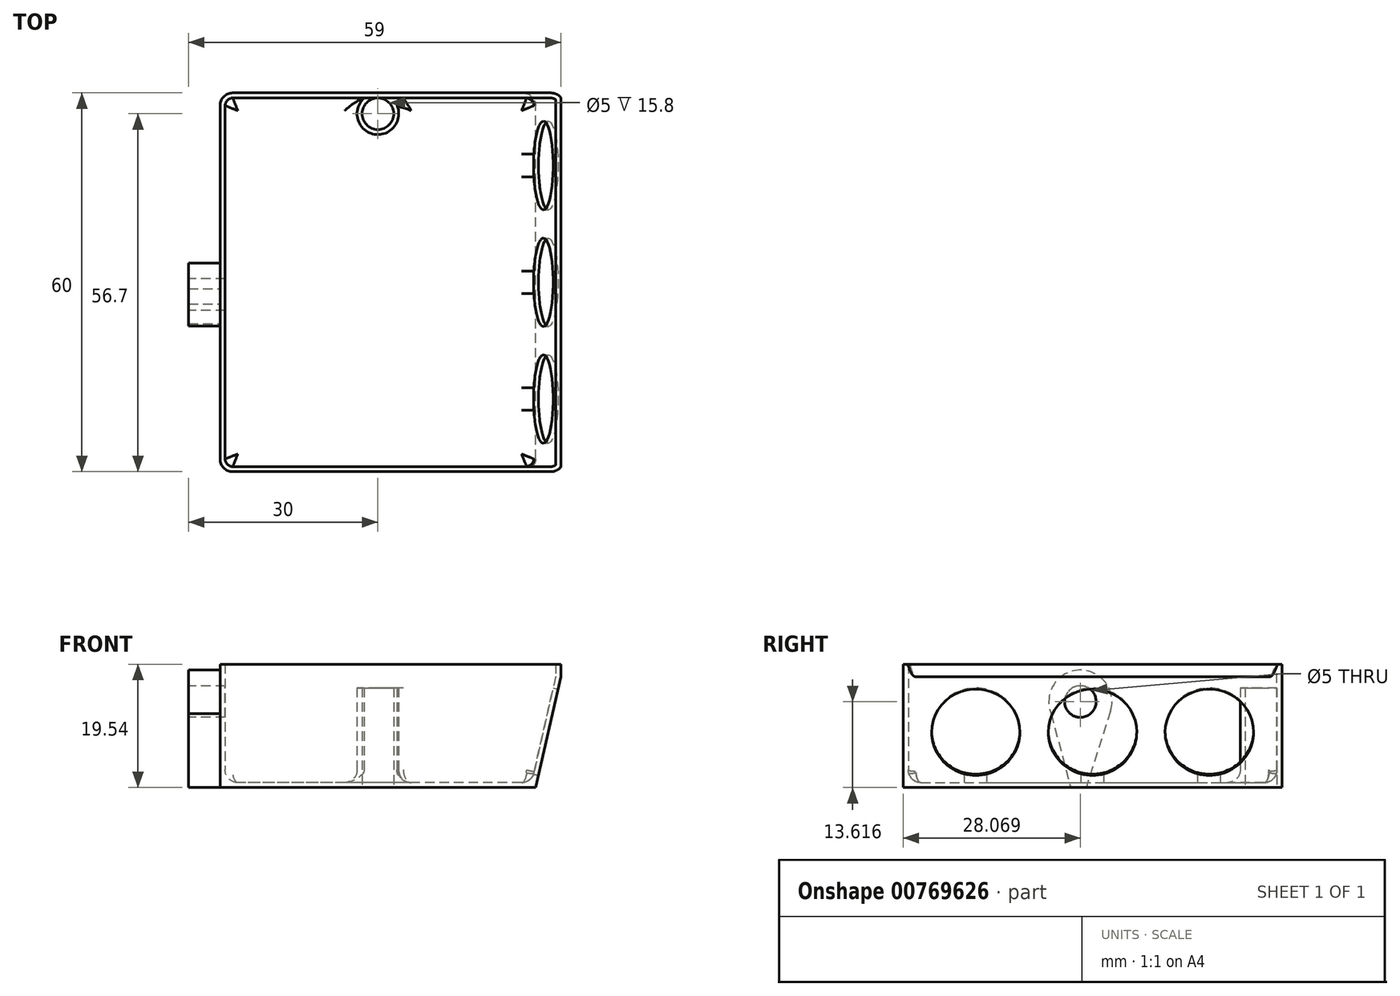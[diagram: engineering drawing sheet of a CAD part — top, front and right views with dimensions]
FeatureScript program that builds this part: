
annotation { "Feature Type Name" : "Feature", "Feature Type Description" : "" }
export const myFeature = defineFeature(function(context is Context, id is Id, definition is map)
    precondition{}
    {
        {
            var Q0;
            Q0=qCreatedBy(makeId("Front.planeOp"),FACE);
            var sketch = newSketch(context, id + "F0", { "sketchPlane" : qUnion([Q0])});
            skLineSegment(sketch, "E0.bottom", {"start": v(25, 9.77) * mm, "end": v(-25, 9.77) * mm});
            skLineSegment(sketch, "E0.top", {"start": v(25, -9.77) * mm, "end": v(-25, -9.77) * mm});
            skLineSegment(sketch, "E0.right", {"start": v(-25, 9.77) * mm, "end": v(-25, -9.77) * mm});
            skPoint(sketch, "E0.middle", {"position": v(0, 0) * mm});
            skLineSegment(sketch, "E1", {"start": v(29, 9.77) * mm, "end": v(25, 9.77) * mm});
            skLineSegment(sketch, "E2", {"start": v(29, 9.77) * mm, "end": v(29, 7.77) * mm});
            skLineSegment(sketch, "E3", {"start": v(29, 7.77) * mm, "end": v(25, -9.77) * mm});
            skSolve(sketch);
        }
        {
            var Q0;
            Q0=makeQuery(id+"F0.imprint","IMPRINT",FACE,{"disambiguationData":[TD([[makeQuery(id+"F0.imprint","IMPRINT",EDGE,{"derivedFrom":sQuery(id+"F0.wireOp",EDGE,"E0.bottom")}),1.0]])]});
            extrude(context, id + "F1", {"entities" : qUnion([Q0]), "depth" : 60 * mm, "offsetDistance" : 25 * mm});
        }
        {
            var Q0;
            Q0=makeQuery(id+"F1.opExtrude","CAP_EDGE",EDGE,{"disambiguationData":[OSD([sQuery(id+"F0.wireOp",EDGE,"E3")])],"isStart":false});
            var Q1;
            Q1=makeQuery(id+"F1.opExtrude","CAP_EDGE",EDGE,{"disambiguationData":[OSD([sQuery(id+"F0.wireOp",EDGE,"E3")])],"isStart":true});
            var Q2;
            Q2=makeQuery(id+"F1.opExtrude","CAP_EDGE",EDGE,{"disambiguationData":[OSD([sQuery(id+"F0.wireOp",EDGE,"E0.right")])],"isStart":true});
            var Q3;
            Q3=makeQuery(id+"F1.opExtrude","CAP_EDGE",EDGE,{"disambiguationData":[OSD([sQuery(id+"F0.wireOp",EDGE,"E0.right")])],"isStart":false});
            fillet(context, id + "F2", {"entities" : qUnion([Q0, Q1, Q2, Q3]), "radius" : 2 * mm, "tangentPropagation" : true, "allowEdgeOverflow" : false});
        }
        {
            var Q0;
            Q0=makeQuery(id+"F1.opExtrude","SWEPT_FACE",FACE,{"disambiguationData":[OSD([sQuery(id+"F0.wireOp",EDGE,"E0.bottom"),sQuery(id+"F0.wireOp",EDGE,"E1")])]});
            shell(context, id + "F3", {"entities" : qUnion([Q0]), "thickness" : 0.8 * mm});
        }
        {
            var Q0;
            Q0=makeQuery(id+"F1.opExtrude","SWEPT_FACE",FACE,{"disambiguationData":[OSD([sQuery(id+"F0.wireOp",EDGE,"E3")])]});
            var sketch = newSketch(context, id + "F4", { "sketchPlane" : qUnion([Q0])});
            skLineSegment(sketch, "E4", {"start": v(-48.5, 5.03) * mm, "end": v(-11.5, 5.03) * mm, "construction": true});
            skLineSegment(sketch, "E5", {"start": v(-30, 5.03) * mm, "end": v(-30, -3.97) * mm, "construction": true});
            skCircle(sketch, "E6", {"center": v(-30, 5.03) * mm, "radius": 7 * mm});
            skCircle(sketch, "E7", {"center": v(-11.5, 5.03) * mm, "radius": 7 * mm});
            skCircle(sketch, "E8", {"center": v(-48.5, 5.03) * mm, "radius": 7 * mm});
            skSolve(sketch);
        }
        {
            var Q0;
            Q0 = qSketchRegion(id + "F4", true);
            extrude(context, id + "F5", {"entities" : qUnion([Q0]), "operationType" : NewBodyOperationType.REMOVE, "endBound" : BoundingType.UP_TO_NEXT, "oppositeDirection" : true, "depth" : 25 * mm, "offsetDistance" : 25 * mm});
        }
        {
            var Q0;
            Q0=makeQuery(id+"F1.opExtrude","SWEPT_FACE",FACE,{"disambiguationData":[OSD([sQuery(id+"F0.wireOp",EDGE,"E0.right")])]});
            var sketch = newSketch(context, id + "F6", { "sketchPlane" : qUnion([Q0])});
            skArc(sketch, "E9", {"start": v(36.56, 1.95) * mm, "mid": v(32.13, 8.84) * mm, "end": v(27.16, 2.34) * mm});
            skLineSegment(sketch, "E10", {"start": v(27.16, 2.34) * mm, "end": v(31, -9.77) * mm});
            skLineSegment(sketch, "E11", {"start": v(36.89, 3.2) * mm, "end": v(33.46, -9.77) * mm});
            skSolve(sketch);
        }
        {
            var Q0;
            Q0 = qSketchRegion(id + "F6", true);
            var Q1;
            {var subQ6=sQuery(id+"F6.wireOp",EDGE,"E10");Q1=makeQuery(id+"F6.imprint","IMPRINT",FACE,{"disambiguationData":[TD([[makeQuery(id+"F6.imprint","IMPRINT",EDGE,{"derivedFrom":subQ6}),1.0]])]});}
            extrude(context, id + "F7", {"entities" : qUnion([Q0, Q1]), "operationType" : NewBodyOperationType.ADD, "depth" : 5 * mm, "offsetDistance" : 25 * mm});
        }
        {
            var Q0;
            Q0=makeQuery(id+"F7.opExtrude","CAP_FACE",FACE,{"disambiguationData":[OSD([sQuery(id+"F0.wireOp",EDGE,"E0.top"),sQuery(id+"F0.wireOp",EDGE,"E0.right"),sQuery(id+"F6.wireOp",EDGE,"E9"),sQuery(id+"F6.wireOp",EDGE,"E10"),sQuery(id+"F6.wireOp",EDGE,"E11")])],"isStart":false});
            var sketch = newSketch(context, id + "F8", { "sketchPlane" : qUnion([Q0])});
            skCircle(sketch, "E12", {"center": v(31.93, 3.85) * mm, "radius": 2.5 * mm});
            skSolve(sketch);
        }
        {
            var Q0;
            Q0 = qSketchRegion(id + "F8", true);
            extrude(context, id + "F9", {"entities" : qUnion([Q0]), "operationType" : NewBodyOperationType.REMOVE, "oppositeDirection" : true, "depth" : 25 * mm, "offsetDistance" : 25 * mm});
        }
        {
            var Q0;
            {var subQ0=sQuery(id+"F0.wireOp",EDGE,"E0.top");Q0=makeQuery(id+"F3.opShell","OFFSET_FACE",FACE,{"disambiguationData":[OSD([subQ0]),TDD([makeQuery(id+"F1.opExtrude","SWEPT_FACE",FACE,{"disambiguationData":[OSD([subQ0])]})])]});}
            var sketch = newSketch(context, id + "F10", { "sketchPlane" : qUnion([Q0])});
            skCircle(sketch, "E13", {"center": v(0, -3.3) * mm, "radius": 2.5 * mm});
            skCircle(sketch, "E14", {"center": v(0, -3.3) * mm, "radius": 3.3 * mm});
            skSolve(sketch);
        }
        {
            var Q0;
            Q0 = qSketchRegion(id + "F10", true);
            var Q1;
            Q1=makeQuery(id+"F1.opExtrude","SWEPT_FACE",FACE,{"disambiguationData":[OSD([sQuery(id+"F0.wireOp",EDGE,"E0.bottom"),sQuery(id+"F0.wireOp",EDGE,"E1")])]});
            extrude(context, id + "F11", {"entities" : qUnion([Q0]), "operationType" : NewBodyOperationType.ADD, "depth" : 15 * mm, "endBoundEntityFace" : qUnion([Q1]), "offsetDistance" : -0.1 * mm});
        }
        {
            var Q0;
            {var subQ0=sQuery(id+"F0.wireOp",EDGE,"E3");var subQ1=sQuery(id+"F0.wireOp",EDGE,"E2");var subQ2=sQuery(id+"F0.wireOp",EDGE,"E1");var subQ3=sQuery(id+"F0.wireOp",EDGE,"E0.right");var subQ4=sQuery(id+"F0.wireOp",EDGE,"E0.top");var subQ5=sQuery(id+"F0.wireOp",EDGE,"E0.bottom");Q0=makeQuery(id+"F11.boolean.opBoolean","INTERSECT",EDGE,{"disambiguationData":[OD(1.0)],"derivedFrom":[makeQuery(id+"F3.opShell","OFFSET_FACE",FACE,{"disambiguationData":[OSD([subQ5,subQ4,subQ3,subQ2,subQ1,subQ0]),TDD([makeQuery(id+"F1.opExtrude","CAP_FACE",FACE,{"disambiguationData":[OSD([subQ5,subQ4,subQ3,subQ2,subQ1,subQ0])],"isStart":true})])]}),makeQuery(id+"F11.opExtrude","SWEPT_FACE",FACE,{"disambiguationData":[OSD([sQuery(id+"F10.wireOp",EDGE,"E14")])]})]});}
            fillet(context, id + "F12", {"entities" : qUnion([Q0]), "radius" : 1 * mm, "tangentPropagation" : true, "allowEdgeOverflow" : false});
        }
        {
            var Q0;
            Q0=makeQuery(id+"F11.opExtrude","CAP_FACE",FACE,{"disambiguationData":[OSD([sQuery(id+"F10.wireOp",EDGE,"E13"),sQuery(id+"F10.wireOp",EDGE,"E14")])],"isStart":false});
            var sketch = newSketch(context, id + "F13", { "sketchPlane" : qUnion([Q0])});
            skCircle(sketch, "E15.0", {"center": v(0, -3.3) * mm, "radius": 2.5 * mm});
            skSolve(sketch);
        }
        {
            var Q0;
            Q0 = qSketchRegion(id + "F13", true);
            extrude(context, id + "F14", {"entities" : qUnion([Q0]), "operationType" : NewBodyOperationType.REMOVE, "oppositeDirection" : true, "depth" : 25 * mm, "offsetDistance" : 25 * mm});
        }
        {
            var Q0;
            {var subQ0=sQuery(id+"F0.wireOp",EDGE,"E3");var subQ1=sQuery(id+"F0.wireOp",EDGE,"E2");var subQ2=sQuery(id+"F0.wireOp",EDGE,"E1");var subQ3=sQuery(id+"F0.wireOp",EDGE,"E0.right");var subQ4=sQuery(id+"F0.wireOp",EDGE,"E0.top");var subQ5=sQuery(id+"F0.wireOp",EDGE,"E0.bottom");Q0=makeQuery(id+"F3.opShell","OFFSET_FACE",FACE,{"disambiguationData":[OSD([subQ5,subQ4,subQ3,subQ2,subQ1,subQ0]),TDD([makeQuery(id+"F1.opExtrude","CAP_FACE",FACE,{"disambiguationData":[OSD([subQ5,subQ4,subQ3,subQ2,subQ1,subQ0])],"isStart":true})])]});}
            var Q1;
            {var subQ0=sQuery(id+"F0.wireOp",EDGE,"E3");var subQ1=sQuery(id+"F0.wireOp",EDGE,"E2");var subQ2=sQuery(id+"F0.wireOp",EDGE,"E1");var subQ3=sQuery(id+"F0.wireOp",EDGE,"E0.right");var subQ4=sQuery(id+"F0.wireOp",EDGE,"E0.top");var subQ5=sQuery(id+"F0.wireOp",EDGE,"E0.bottom");Q1=makeQuery(id+"F3.opShell","OFFSET_FACE",FACE,{"disambiguationData":[OSD([subQ5,subQ4,subQ3,subQ2,subQ1,subQ0]),TDD([makeQuery(id+"F1.opExtrude","CAP_FACE",FACE,{"disambiguationData":[OSD([subQ5,subQ4,subQ3,subQ2,subQ1,subQ0])],"isStart":false})])]});}
            cPlane(context, id + "F15", {"entities" : qUnion([Q0, Q1]), "cplaneType" : CPlaneType.MID_PLANE, "offset" : 25 * mm, "width" : 150 * mm, "height" : 150 * mm});
        }
        {
            var Q0;
            {var subQ0=sQuery(id+"F0.wireOp",EDGE,"E0.right");var subQ1=sQuery(id+"F0.wireOp",EDGE,"E0.top");Q0=makeQuery(id+"Fs4VZ49VYXhLJVG_1.1.F11.boolean.opBoolean","SPLIT",EDGE,{"disambiguationData":[TD([makeQuery(id+"F3.opShell","OFFSET_FACE",FACE,{"disambiguationData":[OSD([subQ0]),TDD([makeQuery(id+"F2.opFillet","BLEND_FACE",FACE,{"disambiguationData":[OSD([subQ0]),TDD([makeQuery(id+"F1.opExtrude","CAP_EDGE",EDGE,{"disambiguationData":[OSD([subQ0])],"isStart":false})])]})])]})])],"derivedFrom":makeQuery(id+"F3.opShell","OFFSET_EDGE",EDGE,{"disambiguationData":[OSD([subQ1]),TDD([makeQuery(id+"F1.opExtrude","CAP_EDGE",EDGE,{"disambiguationData":[OSD([subQ1])],"isStart":false})])]})});}
            var Q1;
            {var subQ0=sQuery(id+"F0.wireOp",EDGE,"E3");var subQ4=sQuery(id+"F0.wireOp",EDGE,"E0.top");Q1=makeQuery(id+"Fs4VZ49VYXhLJVG_1.1.F11.boolean.opBoolean","SPLIT",EDGE,{"disambiguationData":[TD([makeQuery(id+"F3.opShell","OFFSET_FACE",FACE,{"disambiguationData":[OSD([subQ0]),TDD([makeQuery(id+"F2.opFillet","BLEND_FACE",FACE,{"disambiguationData":[OSD([subQ0]),TDD([makeQuery(id+"F1.opExtrude","CAP_EDGE",EDGE,{"disambiguationData":[OSD([subQ0])],"isStart":false})])]})])]})])],"derivedFrom":makeQuery(id+"F3.opShell","OFFSET_EDGE",EDGE,{"disambiguationData":[OSD([subQ4]),TDD([makeQuery(id+"F1.opExtrude","CAP_EDGE",EDGE,{"disambiguationData":[OSD([subQ4])],"isStart":false})])]})});}
            fillet(context, id + "F16", {"entities" : qUnion([Q0, Q1]), "radius" : 2 * mm, "tangentPropagation" : true, "allowEdgeOverflow" : false});
        }
    });
